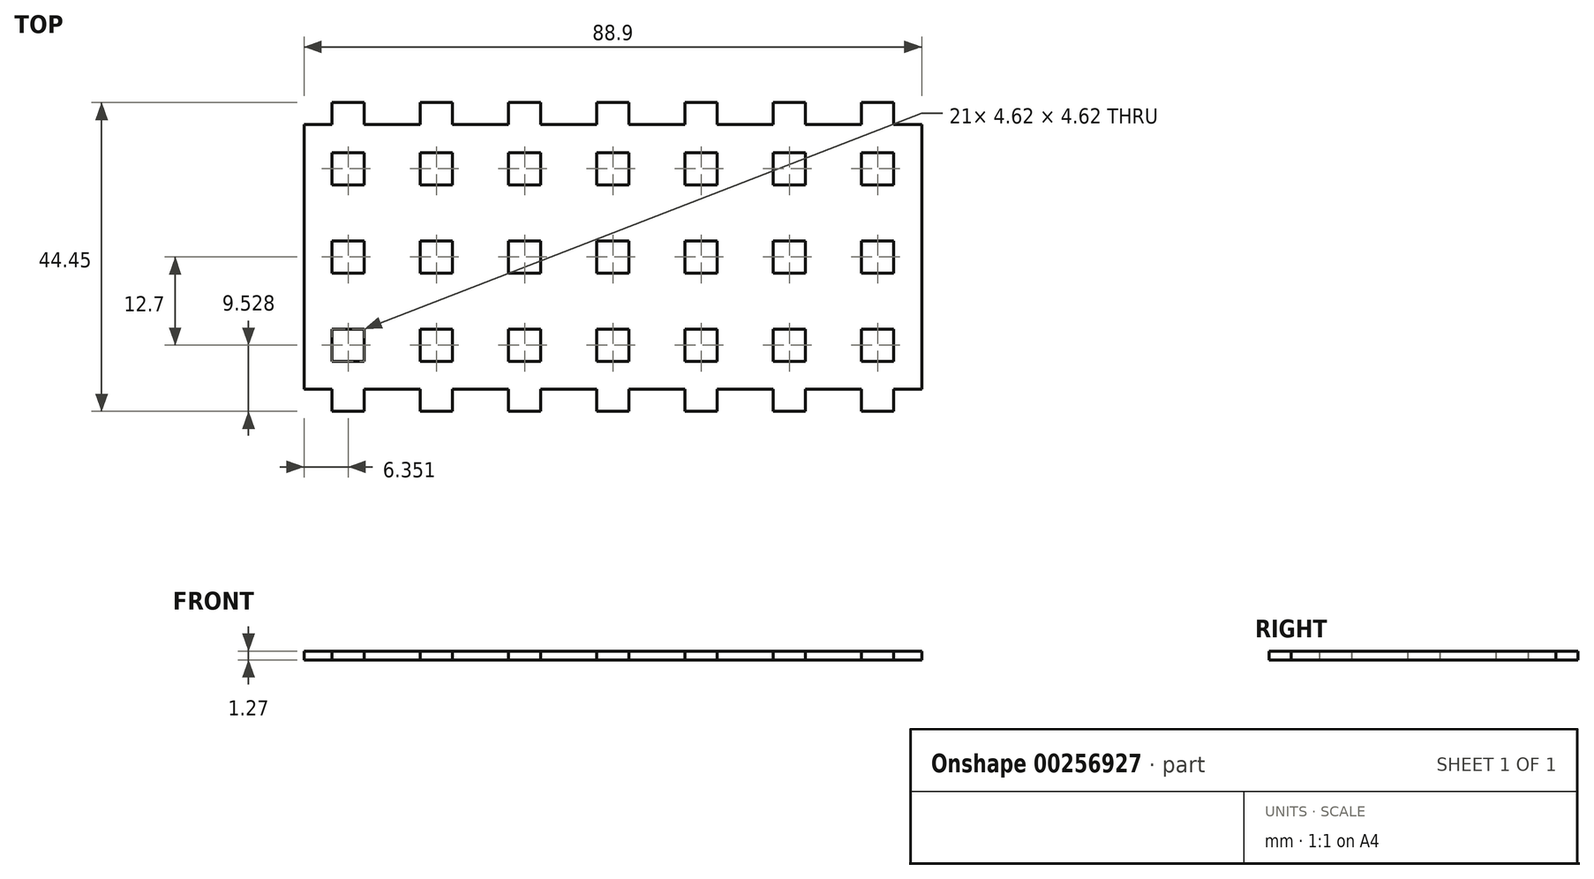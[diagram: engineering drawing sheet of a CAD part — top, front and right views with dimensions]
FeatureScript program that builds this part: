
annotation { "Feature Type Name" : "Feature", "Feature Type Description" : "" }
export const myFeature = defineFeature(function(context is Context, id is Id, definition is map)
    precondition{}
    {
        {
            var Q0;
            Q0=qCreatedBy(makeId("Top.planeOp"),FACE);
            var sketch = newSketch(context, id + "F0", { "sketchPlane" : qUnion([Q0])});
            skLineSegment(sketch, "E0.bottom", {"start": v(78.03, -1.57) * mm, "end": v(74, -1.57) * mm});
            skLineSegment(sketch, "E0.top", {"start": v(78.03, -39.67) * mm, "end": v(74, -39.67) * mm});
            skLineSegment(sketch, "E0.left", {"start": v(78.03, -1.57) * mm, "end": v(78.03, -39.67) * mm});
            skLineSegment(sketch, "E0.right", {"start": v(-10.87, -1.57) * mm, "end": v(-10.87, -39.67) * mm});
            skLineSegment(sketch, "E1", {"start": v(-10.87, -39.67) * mm, "end": v(-4.52, -39.67) * mm});
            skLineSegment(sketch, "E2.top", {"start": v(-2.2, -42.85) * mm, "end": v(-6.83, -42.85) * mm});
            skLineSegment(sketch, "E2.left", {"start": v(-2.2, -39.67) * mm, "end": v(-2.2, -42.85) * mm});
            skLineSegment(sketch, "E2.right", {"start": v(-6.83, -39.67) * mm, "end": v(-6.83, -42.85) * mm});
            skPoint(sketch, "E2.middle", {"position": v(-4.52, -39.67) * mm});
            skPoint(sketch, "E2.bottom.start.orphan", {"position": v(-2.2, -36.5) * mm});
            skPoint(sketch, "E3.orphan", {"position": v(-6.83, -36.5) * mm});
            skLineSegment(sketch, "E4.1.0.0", {"start": v(10.5, -39.67) * mm, "end": v(10.5, -42.85) * mm});
            skLineSegment(sketch, "E4.1.0.1", {"start": v(5.87, -39.67) * mm, "end": v(5.87, -42.85) * mm});
            skLineSegment(sketch, "E4.1.0.2", {"start": v(10.5, -42.85) * mm, "end": v(5.87, -42.85) * mm});
            skLineSegment(sketch, "E4.2.0.0", {"start": v(23.2, -39.67) * mm, "end": v(23.2, -42.85) * mm});
            skLineSegment(sketch, "E4.2.0.1", {"start": v(18.57, -39.67) * mm, "end": v(18.57, -42.85) * mm});
            skLineSegment(sketch, "E4.2.0.2", {"start": v(23.2, -42.85) * mm, "end": v(18.57, -42.85) * mm});
            skLineSegment(sketch, "E4.3.0.0", {"start": v(35.9, -39.67) * mm, "end": v(35.9, -42.85) * mm});
            skLineSegment(sketch, "E4.3.0.1", {"start": v(31.27, -39.67) * mm, "end": v(31.27, -42.85) * mm});
            skLineSegment(sketch, "E4.3.0.2", {"start": v(35.9, -42.85) * mm, "end": v(31.27, -42.85) * mm});
            skLineSegment(sketch, "E4.4.0.0", {"start": v(48.6, -39.67) * mm, "end": v(48.6, -42.85) * mm});
            skLineSegment(sketch, "E4.4.0.1", {"start": v(43.97, -39.67) * mm, "end": v(43.97, -42.85) * mm});
            skLineSegment(sketch, "E4.4.0.2", {"start": v(48.6, -42.85) * mm, "end": v(43.97, -42.85) * mm});
            skLineSegment(sketch, "E4.5.0.0", {"start": v(61.3, -39.67) * mm, "end": v(61.3, -42.85) * mm});
            skLineSegment(sketch, "E4.5.0.1", {"start": v(56.67, -39.67) * mm, "end": v(56.67, -42.85) * mm});
            skLineSegment(sketch, "E4.5.0.2", {"start": v(61.3, -42.85) * mm, "end": v(56.67, -42.85) * mm});
            skLineSegment(sketch, "E4.6.0.0", {"start": v(74, -39.67) * mm, "end": v(74, -42.85) * mm});
            skLineSegment(sketch, "E4.6.0.1", {"start": v(69.37, -39.67) * mm, "end": v(69.37, -42.85) * mm});
            skLineSegment(sketch, "E4.6.0.2", {"start": v(74, -42.85) * mm, "end": v(69.37, -42.85) * mm});
            skLineSegment(sketch, "E4.direction1", {"start": v(5.87, -42.85) * mm, "end": v(10.5, -42.85) * mm, "construction": true});
            skLineSegment(sketch, "E5.MirrorCS", {"start": v(31.27, -1.57) * mm, "end": v(31.27, 1.6) * mm});
            skLineSegment(sketch, "E6.MirrorCS", {"start": v(69.37, -1.57) * mm, "end": v(69.37, 1.6) * mm});
            skLineSegment(sketch, "E7.MirrorCS", {"start": v(48.6, -1.57) * mm, "end": v(48.6, 1.6) * mm});
            skLineSegment(sketch, "E8.MirrorCS", {"start": v(23.2, -1.57) * mm, "end": v(23.2, 1.6) * mm});
            skLineSegment(sketch, "E9.MirrorCS", {"start": v(18.57, -1.57) * mm, "end": v(18.57, 1.6) * mm});
            skLineSegment(sketch, "E10.MirrorCS", {"start": v(74, -1.57) * mm, "end": v(74, 1.6) * mm});
            skLineSegment(sketch, "E11.MirrorCS", {"start": v(61.3, -1.57) * mm, "end": v(61.3, 1.6) * mm});
            skLineSegment(sketch, "E12.MirrorCS", {"start": v(-10.87, -1.57) * mm, "end": v(-6.83, -1.57) * mm});
            skLineSegment(sketch, "E13.MirrorCS", {"start": v(-2.2, -1.57) * mm, "end": v(-2.2, 1.6) * mm});
            skLineSegment(sketch, "E14.MirrorCS", {"start": v(-6.83, -1.57) * mm, "end": v(-6.83, 1.6) * mm});
            skLineSegment(sketch, "E15.MirrorCS", {"start": v(10.5, -1.57) * mm, "end": v(10.5, 1.6) * mm});
            skLineSegment(sketch, "E16.MirrorCS", {"start": v(35.9, -1.57) * mm, "end": v(35.9, 1.6) * mm});
            skLineSegment(sketch, "E17.MirrorCS", {"start": v(56.67, -1.57) * mm, "end": v(56.67, 1.6) * mm});
            skLineSegment(sketch, "E18.MirrorCS", {"start": v(43.97, -1.57) * mm, "end": v(43.97, 1.6) * mm});
            skLineSegment(sketch, "E19.MirrorCS", {"start": v(10.5, 1.6) * mm, "end": v(5.87, 1.6) * mm});
            skLineSegment(sketch, "E20.MirrorCS", {"start": v(5.87, -1.57) * mm, "end": v(5.87, 1.6) * mm});
            skLineSegment(sketch, "E21.MirrorCS", {"start": v(23.2, 1.6) * mm, "end": v(18.57, 1.6) * mm});
            skLineSegment(sketch, "E22.MirrorCS", {"start": v(35.9, 1.6) * mm, "end": v(31.27, 1.6) * mm});
            skLineSegment(sketch, "E23.MirrorCS", {"start": v(-2.2, 1.6) * mm, "end": v(-6.83, 1.6) * mm});
            skLineSegment(sketch, "E24.MirrorCS", {"start": v(48.6, 1.6) * mm, "end": v(43.97, 1.6) * mm});
            skLineSegment(sketch, "E25.MirrorCS", {"start": v(61.3, 1.6) * mm, "end": v(56.67, 1.6) * mm});
            skLineSegment(sketch, "E26.MirrorCS", {"start": v(5.87, 1.6) * mm, "end": v(10.5, 1.6) * mm, "construction": true});
            skLineSegment(sketch, "E27.MirrorCS", {"start": v(74, 1.6) * mm, "end": v(69.37, 1.6) * mm});
            skLineSegment(sketch, "E28.left", {"start": v(-10.87, -39.67) * mm, "end": v(-10.87, -33.32) * mm});
            skLineSegment(sketch, "E29.bottom", {"start": v(-2.2, -35.63) * mm, "end": v(-6.83, -35.63) * mm});
            skLineSegment(sketch, "E29.top", {"start": v(-2.2, -31.01) * mm, "end": v(-6.83, -31.01) * mm});
            skLineSegment(sketch, "E29.left", {"start": v(-2.2, -35.63) * mm, "end": v(-2.2, -31.01) * mm});
            skLineSegment(sketch, "E29.right", {"start": v(-6.83, -35.63) * mm, "end": v(-6.83, -31.01) * mm});
            skPoint(sketch, "E29.middle", {"position": v(-4.52, -33.32) * mm});
            skLineSegment(sketch, "E30.1.0.0", {"start": v(10.5, -31.01) * mm, "end": v(5.87, -31.01) * mm});
            skLineSegment(sketch, "E30.1.0.1", {"start": v(5.87, -35.63) * mm, "end": v(5.87, -31.01) * mm});
            skLineSegment(sketch, "E30.1.0.2", {"start": v(10.5, -35.63) * mm, "end": v(5.87, -35.63) * mm});
            skLineSegment(sketch, "E30.1.0.3", {"start": v(10.5, -35.63) * mm, "end": v(10.5, -31.01) * mm});
            skLineSegment(sketch, "E30.2.0.0", {"start": v(23.2, -31.01) * mm, "end": v(18.57, -31.01) * mm});
            skLineSegment(sketch, "E30.2.0.1", {"start": v(18.57, -35.63) * mm, "end": v(18.57, -31.01) * mm});
            skLineSegment(sketch, "E30.2.0.2", {"start": v(23.2, -35.63) * mm, "end": v(18.57, -35.63) * mm});
            skLineSegment(sketch, "E30.2.0.3", {"start": v(23.2, -35.63) * mm, "end": v(23.2, -31.01) * mm});
            skLineSegment(sketch, "E30.3.0.0", {"start": v(35.9, -31.01) * mm, "end": v(31.27, -31.01) * mm});
            skLineSegment(sketch, "E30.3.0.1", {"start": v(31.27, -35.63) * mm, "end": v(31.27, -31.01) * mm});
            skLineSegment(sketch, "E30.3.0.2", {"start": v(35.9, -35.63) * mm, "end": v(31.27, -35.63) * mm});
            skLineSegment(sketch, "E30.3.0.3", {"start": v(35.9, -35.63) * mm, "end": v(35.9, -31.01) * mm});
            skLineSegment(sketch, "E30.4.0.0", {"start": v(48.6, -31.01) * mm, "end": v(43.97, -31.01) * mm});
            skLineSegment(sketch, "E30.4.0.1", {"start": v(43.97, -35.63) * mm, "end": v(43.97, -31.01) * mm});
            skLineSegment(sketch, "E30.4.0.2", {"start": v(48.6, -35.63) * mm, "end": v(43.97, -35.63) * mm});
            skLineSegment(sketch, "E30.4.0.3", {"start": v(48.6, -35.63) * mm, "end": v(48.6, -31.01) * mm});
            skLineSegment(sketch, "E30.5.0.0", {"start": v(61.3, -31.01) * mm, "end": v(56.67, -31.01) * mm});
            skLineSegment(sketch, "E30.5.0.1", {"start": v(56.67, -35.63) * mm, "end": v(56.67, -31.01) * mm});
            skLineSegment(sketch, "E30.5.0.2", {"start": v(61.3, -35.63) * mm, "end": v(56.67, -35.63) * mm});
            skLineSegment(sketch, "E30.5.0.3", {"start": v(61.3, -35.63) * mm, "end": v(61.3, -31.01) * mm});
            skLineSegment(sketch, "E30.6.0.0", {"start": v(74, -31.01) * mm, "end": v(69.37, -31.01) * mm});
            skLineSegment(sketch, "E30.6.0.1", {"start": v(69.37, -35.63) * mm, "end": v(69.37, -31.01) * mm});
            skLineSegment(sketch, "E30.6.0.2", {"start": v(74, -35.63) * mm, "end": v(69.37, -35.63) * mm});
            skLineSegment(sketch, "E30.6.0.3", {"start": v(74, -35.63) * mm, "end": v(74, -31.01) * mm});
            skLineSegment(sketch, "E30.direction1", {"start": v(-6.83, -31.01) * mm, "end": v(-2.2, -31.01) * mm, "construction": true});
            skPoint(sketch, "E31.0.1.0", {"position": v(-6.83, -23.8) * mm});
            skPoint(sketch, "E31.0.1.1", {"position": v(-4.52, -20.62) * mm});
            skLineSegment(sketch, "E31.0.1.2", {"start": v(61.3, -18.31) * mm, "end": v(56.67, -18.31) * mm});
            skLineSegment(sketch, "E31.0.1.3", {"start": v(35.9, -22.93) * mm, "end": v(35.9, -18.31) * mm});
            skLineSegment(sketch, "E31.0.1.4", {"start": v(-6.83, -22.93) * mm, "end": v(-6.83, -18.31) * mm});
            skLineSegment(sketch, "E31.0.1.5", {"start": v(10.5, -22.93) * mm, "end": v(5.87, -22.93) * mm});
            skLineSegment(sketch, "E31.0.1.6", {"start": v(35.9, -22.93) * mm, "end": v(31.27, -22.93) * mm});
            skLineSegment(sketch, "E31.0.1.7", {"start": v(23.2, -22.93) * mm, "end": v(23.2, -18.31) * mm});
            skLineSegment(sketch, "E31.0.1.8", {"start": v(10.5, -18.31) * mm, "end": v(5.87, -18.31) * mm});
            skLineSegment(sketch, "E31.0.1.9", {"start": v(23.2, -22.93) * mm, "end": v(18.57, -22.93) * mm});
            skPoint(sketch, "E31.0.1.10", {"position": v(-2.2, -23.8) * mm});
            skLineSegment(sketch, "E31.0.1.11", {"start": v(48.6, -18.31) * mm, "end": v(43.97, -18.31) * mm});
            skLineSegment(sketch, "E31.0.1.12", {"start": v(48.6, -22.93) * mm, "end": v(48.6, -18.31) * mm});
            skLineSegment(sketch, "E31.0.1.13", {"start": v(43.97, -22.93) * mm, "end": v(43.97, -18.31) * mm});
            skLineSegment(sketch, "E31.0.1.14", {"start": v(35.9, -18.31) * mm, "end": v(31.27, -18.31) * mm});
            skLineSegment(sketch, "E31.0.1.15", {"start": v(-6.83, -18.31) * mm, "end": v(-2.2, -18.31) * mm, "construction": true});
            skLineSegment(sketch, "E31.0.1.16", {"start": v(-2.2, -22.93) * mm, "end": v(-2.2, -18.31) * mm});
            skLineSegment(sketch, "E31.0.1.17", {"start": v(61.3, -22.93) * mm, "end": v(56.67, -22.93) * mm});
            skLineSegment(sketch, "E31.0.1.18", {"start": v(31.27, -22.93) * mm, "end": v(31.27, -18.31) * mm});
            skLineSegment(sketch, "E31.0.1.19", {"start": v(74, -22.93) * mm, "end": v(74, -18.31) * mm});
            skLineSegment(sketch, "E31.0.1.20", {"start": v(48.6, -22.93) * mm, "end": v(43.97, -22.93) * mm});
            skLineSegment(sketch, "E31.0.1.21", {"start": v(5.87, -22.93) * mm, "end": v(5.87, -18.31) * mm});
            skLineSegment(sketch, "E31.0.1.22", {"start": v(74, -18.31) * mm, "end": v(69.37, -18.31) * mm});
            skLineSegment(sketch, "E31.0.1.23", {"start": v(23.2, -18.31) * mm, "end": v(18.57, -18.31) * mm});
            skLineSegment(sketch, "E31.0.1.24", {"start": v(56.67, -22.93) * mm, "end": v(56.67, -18.31) * mm});
            skLineSegment(sketch, "E31.0.1.25", {"start": v(10.5, -22.93) * mm, "end": v(10.5, -18.31) * mm});
            skLineSegment(sketch, "E31.0.1.26", {"start": v(61.3, -22.93) * mm, "end": v(61.3, -18.31) * mm});
            skLineSegment(sketch, "E31.0.1.27", {"start": v(69.37, -22.93) * mm, "end": v(69.37, -18.31) * mm});
            skLineSegment(sketch, "E31.0.1.28", {"start": v(18.57, -22.93) * mm, "end": v(18.57, -18.31) * mm});
            skLineSegment(sketch, "E31.0.1.29", {"start": v(74, -22.93) * mm, "end": v(69.37, -22.93) * mm});
            skLineSegment(sketch, "E31.0.1.30", {"start": v(-2.2, -22.93) * mm, "end": v(-6.83, -22.93) * mm});
            skLineSegment(sketch, "E31.0.1.31", {"start": v(-2.2, -18.31) * mm, "end": v(-6.83, -18.31) * mm});
            skPoint(sketch, "E31.0.2.0", {"position": v(-6.83, -11.1) * mm});
            skPoint(sketch, "E31.0.2.1", {"position": v(-4.52, -7.92) * mm});
            skLineSegment(sketch, "E31.0.2.2", {"start": v(61.3, -5.61) * mm, "end": v(56.67, -5.61) * mm});
            skLineSegment(sketch, "E31.0.2.3", {"start": v(35.9, -10.23) * mm, "end": v(35.9, -5.61) * mm});
            skLineSegment(sketch, "E31.0.2.4", {"start": v(-6.83, -10.23) * mm, "end": v(-6.83, -5.61) * mm});
            skLineSegment(sketch, "E31.0.2.5", {"start": v(10.5, -10.23) * mm, "end": v(5.87, -10.23) * mm});
            skLineSegment(sketch, "E31.0.2.6", {"start": v(35.9, -10.23) * mm, "end": v(31.27, -10.23) * mm});
            skLineSegment(sketch, "E31.0.2.7", {"start": v(23.2, -10.23) * mm, "end": v(23.2, -5.61) * mm});
            skLineSegment(sketch, "E31.0.2.8", {"start": v(10.5, -5.61) * mm, "end": v(5.87, -5.61) * mm});
            skLineSegment(sketch, "E31.0.2.9", {"start": v(23.2, -10.23) * mm, "end": v(18.57, -10.23) * mm});
            skPoint(sketch, "E31.0.2.10", {"position": v(-2.2, -11.1) * mm});
            skLineSegment(sketch, "E31.0.2.11", {"start": v(48.6, -5.61) * mm, "end": v(43.97, -5.61) * mm});
            skLineSegment(sketch, "E31.0.2.12", {"start": v(48.6, -10.23) * mm, "end": v(48.6, -5.61) * mm});
            skLineSegment(sketch, "E31.0.2.13", {"start": v(43.97, -10.23) * mm, "end": v(43.97, -5.61) * mm});
            skLineSegment(sketch, "E31.0.2.14", {"start": v(35.9, -5.61) * mm, "end": v(31.27, -5.61) * mm});
            skLineSegment(sketch, "E31.0.2.15", {"start": v(-6.83, -5.61) * mm, "end": v(-2.2, -5.61) * mm, "construction": true});
            skLineSegment(sketch, "E31.0.2.16", {"start": v(-2.2, -10.23) * mm, "end": v(-2.2, -5.61) * mm});
            skLineSegment(sketch, "E31.0.2.17", {"start": v(61.3, -10.23) * mm, "end": v(56.67, -10.23) * mm});
            skLineSegment(sketch, "E31.0.2.18", {"start": v(31.27, -10.23) * mm, "end": v(31.27, -5.61) * mm});
            skLineSegment(sketch, "E31.0.2.19", {"start": v(74, -10.23) * mm, "end": v(74, -5.61) * mm});
            skLineSegment(sketch, "E31.0.2.20", {"start": v(48.6, -10.23) * mm, "end": v(43.97, -10.23) * mm});
            skLineSegment(sketch, "E31.0.2.21", {"start": v(5.87, -10.23) * mm, "end": v(5.87, -5.61) * mm});
            skLineSegment(sketch, "E31.0.2.22", {"start": v(74, -5.61) * mm, "end": v(69.37, -5.61) * mm});
            skLineSegment(sketch, "E31.0.2.23", {"start": v(23.2, -5.61) * mm, "end": v(18.57, -5.61) * mm});
            skLineSegment(sketch, "E31.0.2.24", {"start": v(56.67, -10.23) * mm, "end": v(56.67, -5.61) * mm});
            skLineSegment(sketch, "E31.0.2.25", {"start": v(10.5, -10.23) * mm, "end": v(10.5, -5.61) * mm});
            skLineSegment(sketch, "E31.0.2.26", {"start": v(61.3, -10.23) * mm, "end": v(61.3, -5.61) * mm});
            skLineSegment(sketch, "E31.0.2.27", {"start": v(69.37, -10.23) * mm, "end": v(69.37, -5.61) * mm});
            skLineSegment(sketch, "E31.0.2.28", {"start": v(18.57, -10.23) * mm, "end": v(18.57, -5.61) * mm});
            skLineSegment(sketch, "E31.0.2.29", {"start": v(74, -10.23) * mm, "end": v(69.37, -10.23) * mm});
            skLineSegment(sketch, "E31.0.2.30", {"start": v(-2.2, -10.23) * mm, "end": v(-6.83, -10.23) * mm});
            skLineSegment(sketch, "E31.0.2.31", {"start": v(-2.2, -5.61) * mm, "end": v(-6.83, -5.61) * mm});
            skLineSegment(sketch, "E31.direction2", {"start": v(-6.83, -36.5) * mm, "end": v(-6.83, -35.63) * mm, "construction": true});
            skLineSegment(sketch, "E32.trimOffspring", {"start": v(69.37, -1.57) * mm, "end": v(61.3, -1.57) * mm});
            skLineSegment(sketch, "E33.trimOffspring", {"start": v(56.67, -1.57) * mm, "end": v(48.6, -1.57) * mm});
            skLineSegment(sketch, "E34.trimOffspring", {"start": v(31.27, -1.57) * mm, "end": v(23.2, -1.57) * mm});
            skLineSegment(sketch, "E35.trimOffspring", {"start": v(18.57, -1.57) * mm, "end": v(10.5, -1.57) * mm});
            skLineSegment(sketch, "E36.trimOffspring", {"start": v(5.87, -1.57) * mm, "end": v(-2.2, -1.57) * mm});
            skLineSegment(sketch, "E37.trimOffspring", {"start": v(-6.83, -1.57) * mm, "end": v(-10.87, -1.57) * mm});
            skLineSegment(sketch, "E38.trimOffspring", {"start": v(43.97, -1.57) * mm, "end": v(35.9, -1.57) * mm});
            skLineSegment(sketch, "E39.trimOffspring", {"start": v(69.37, -39.67) * mm, "end": v(61.3, -39.67) * mm});
            skLineSegment(sketch, "E40.trimOffspring", {"start": v(56.67, -39.67) * mm, "end": v(48.6, -39.67) * mm});
            skLineSegment(sketch, "E41.trimOffspring", {"start": v(43.97, -39.67) * mm, "end": v(35.9, -39.67) * mm});
            skLineSegment(sketch, "E42.trimOffspring", {"start": v(31.27, -39.67) * mm, "end": v(23.2, -39.67) * mm});
            skLineSegment(sketch, "E43.trimOffspring", {"start": v(18.57, -39.67) * mm, "end": v(10.5, -39.67) * mm});
            skLineSegment(sketch, "E44.trimOffspring", {"start": v(5.87, -39.67) * mm, "end": v(-2.2, -39.67) * mm});
            skLineSegment(sketch, "E45.trimOffspring", {"start": v(-6.83, -39.67) * mm, "end": v(-10.87, -39.67) * mm});
            skSolve(sketch);
        }
        {
            var Q0;
            Q0 = qSketchRegion(id + "F0", true);
            extrude(context, id + "F1", {"entities" : qUnion([Q0]), "depth" : 1.27 * mm});
        }
    });
